# Revit family: 6983 Стальной фонарный столб Т-22 со светильником Хоббика
name_source: partatom
category: Антураж
revit_build: Autodesk Revit 2018 (Build: 20180423_1000(x64)
units: mm (PartAtom-declared; Revit-internal decimal feet)

## family parameters
Всегда вертикально = Да
Источник визуального образа = Геометрия семейства
На основе рабочей плоскости = Нет
Общий = Нет
При загрузке вырезать с полостями = Нет
Точка расчета площади = Нет

## types (6) — shared parameters
URL = https://hobbyka.ru
Артикул товара = Арт. 6983
Группа модели = Светильники со стальными опорами
Длина = 805 мм
Изготовитель = ООО «Хоббика»
Изображение типоразмера = Стальной фонарный столб Т-22 со светильником Арт 6983.jpg
Материал изделия = Сталь
Цвет каркаса = Сталь
Ширина = 400 мм

## per-type parameters (varying)
| type | Версия 3,516 м | Версия 4,016 м | Версия 4,516 м | Версия 5,016 м | Версия 5,516 м | Версия 6,016 м | Высота | Описание |
| Версия 3,516 м | Да | Нет | Нет | Нет | Нет | Нет | 3516 мм | Стальной фонарный столб Т-22 со светильником. Версия 3,516 м |
| Версия 4,016 м | Нет | Да | Нет | Нет | Нет | Нет | 4016 мм | Стальной фонарный столб Т-22 со светильником. Версия 4,016 м |
| Версия 4,516 м | Нет | Нет | Да | Нет | Нет | Нет | 4516 мм | Стальной фонарный столб Т-22 со светильником. Версия 4,516 м |
| Версия 5,016 м | Нет | Нет | Нет | Да | Нет | Нет | 5016 мм | Стальной фонарный столб Т-22 со светильником. Версия 5,016 м |
| Версия 5,516 м | Нет | Нет | Нет | Нет | Да | Нет | 5516 мм | Стальной фонарный столб Т-22 со светильником. Версия 5,516 м |
| Версия 6,016 м | Нет | Нет | Нет | Нет | Нет | Да | 6016 мм | Стальной фонарный столб Т-22 со светильником. Версия 6,016 м |
